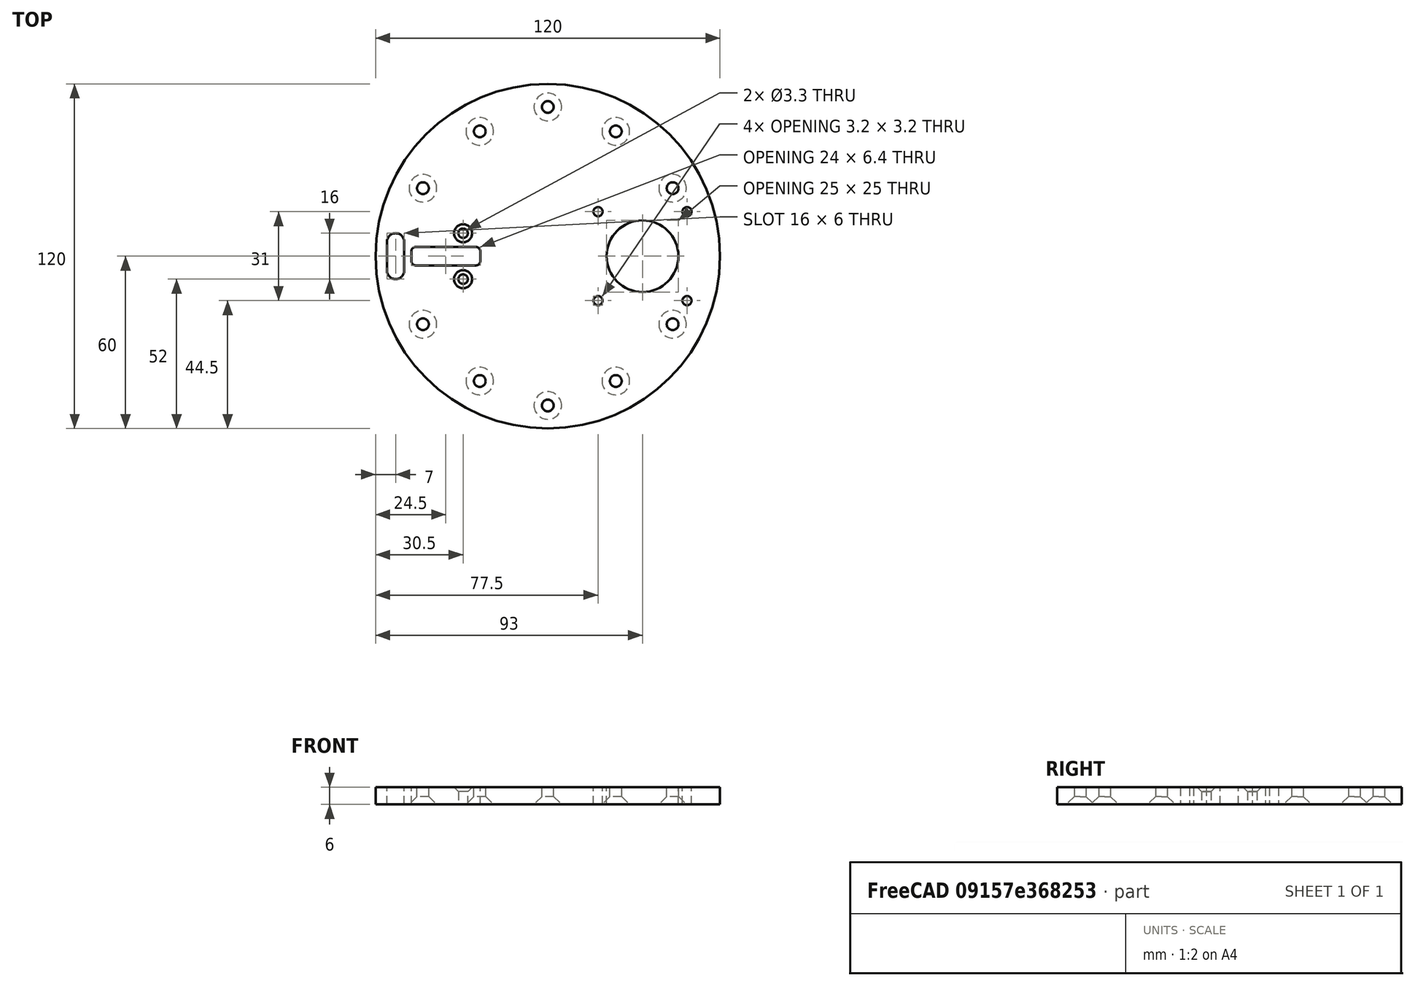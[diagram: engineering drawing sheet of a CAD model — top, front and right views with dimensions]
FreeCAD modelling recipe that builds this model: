
FCSTD DOCUMENT  (FreeCAD 0.19R24276 (Git))
Label: Z-axis_top_plate
License: All rights reserved
LicenseURL: http://en.wikipedia.org/wiki/All_rights_reserved
objects: Part::Part2DObjectPython×2, PartDesign::Chamfer×2, Sketcher::SketchObject×1, PartDesign::Pad×1, PartDesign::Fillet×1, PartDesign::Body×1
note: 12 computed .brp shape members not serialized (recipe doc carries the construction recipe); baked Part::Feature solids carry a one-line shape summary decoded from their .brp

FEATURE [Part::Part2DObjectPython] Shape2DView  # Draft 2D object (typed FeaturePython)
  FaceNumbers = [32]
  FuseArch = false
  HiddenLines = false
  InPlace = true
  Projection = (0,1,0)
  ProjectionMode = 0
  SegmentLength = 0.05
  Tessellation = false
  VisibleOnly = false
FEATURE [Sketcher::SketchObject] Sketch
  FullyConstrained = false
  MapMode = 5
  Support = -> [XY_Plane]
  sketch-geometry (42):
    g0: ArcOfCircle CenterX=0 CenterY=-52 CenterZ=0 NormalX=0 NormalY=0 NormalZ=1 AngleXU=0 Radius=2.05 StartAngle=3.14159 EndAngle=6.28319
    g1: ArcOfCircle CenterX=23.6881 CenterY=-43.4871 CenterZ=0 NormalX=0 NormalY=0 NormalZ=1 AngleXU=0 Radius=2.05 StartAngle=3.14159 EndAngle=6.28319
    g2: ArcOfCircle CenterX=43.4871 CenterY=-23.6881 CenterZ=0 NormalX=0 NormalY=0 NormalZ=1 AngleXU=0 Radius=2.05 StartAngle=3.14159 EndAngle=6.28319
    g3: ArcOfCircle CenterX=43.4871 CenterY=23.6881 CenterZ=0 NormalX=0 NormalY=0 NormalZ=1 AngleXU=0 Radius=2.05 StartAngle=3.14159 EndAngle=6.28319
    g4: ArcOfCircle CenterX=23.6881 CenterY=43.4871 CenterZ=0 NormalX=0 NormalY=0 NormalZ=1 AngleXU=0 Radius=2.05 StartAngle=3.14159 EndAngle=6.28319
    g5: ArcOfCircle CenterX=0 CenterY=52 CenterZ=0 NormalX=0 NormalY=0 NormalZ=1 AngleXU=0 Radius=2.05 StartAngle=3.14159 EndAngle=6.28319
    g6: ArcOfCircle CenterX=-23.6881 CenterY=43.4871 CenterZ=0 NormalX=0 NormalY=0 NormalZ=1 AngleXU=0 Radius=2.05 StartAngle=3.14159 EndAngle=6.28319
    g7: ArcOfCircle CenterX=-43.4871 CenterY=23.6881 CenterZ=0 NormalX=0 NormalY=0 NormalZ=1 AngleXU=0 Radius=2.05 StartAngle=3.14159 EndAngle=6.28319
    g8: ArcOfCircle CenterX=-43.4871 CenterY=-23.6881 CenterZ=0 NormalX=0 NormalY=0 NormalZ=1 AngleXU=0 Radius=2.05 StartAngle=3.14159 EndAngle=6.28319
    g9: ArcOfCircle CenterX=-23.6881 CenterY=-43.4871 CenterZ=0 NormalX=0 NormalY=0 NormalZ=1 AngleXU=0 Radius=2.05 StartAngle=3.14159 EndAngle=6.28319
    g10: ArcOfCircle CenterX=17.5 CenterY=-15.5 CenterZ=0 NormalX=0 NormalY=0 NormalZ=1 AngleXU=0 Radius=1.6 StartAngle=3.14159 EndAngle=6.28319
    g11: ArcOfCircle CenterX=17.5 CenterY=15.5 CenterZ=0 NormalX=0 NormalY=0 NormalZ=1 AngleXU=0 Radius=1.6 StartAngle=3.14159 EndAngle=6.28319
    g12: ArcOfCircle CenterX=48.5 CenterY=15.5 CenterZ=0 NormalX=0 NormalY=0 NormalZ=1 AngleXU=0 Radius=1.6 StartAngle=3.14159 EndAngle=6.28319
    g13: ArcOfCircle CenterX=48.5 CenterY=-15.5 CenterZ=0 NormalX=0 NormalY=0 NormalZ=1 AngleXU=0 Radius=1.6 StartAngle=3.14159 EndAngle=6.28319
    g14: ArcOfCircle CenterX=33 CenterY=0 CenterZ=0 NormalX=0 NormalY=0 NormalZ=1 AngleXU=0 Radius=12.5 StartAngle=3.14159 EndAngle=6.28319
    g15: ArcOfCircle CenterX=0 CenterY=0 CenterZ=0 NormalX=0 NormalY=0 NormalZ=1 AngleXU=0 Radius=60 StartAngle=0 EndAngle=3.14159
    g16: ArcOfCircle CenterX=0 CenterY=0 CenterZ=0 NormalX=0 NormalY=0 NormalZ=1 AngleXU=0 Radius=60 StartAngle=3.14159 EndAngle=6.28319
    g17: ArcOfCircle CenterX=17.5 CenterY=-15.5 CenterZ=0 NormalX=0 NormalY=0 NormalZ=1 AngleXU=0 Radius=1.6 StartAngle=0 EndAngle=3.14159
    g18: ArcOfCircle CenterX=17.5 CenterY=15.5 CenterZ=0 NormalX=0 NormalY=0 NormalZ=1 AngleXU=0 Radius=1.6 StartAngle=0 EndAngle=3.14159
    g19: ArcOfCircle CenterX=48.5 CenterY=15.5 CenterZ=0 NormalX=0 NormalY=0 NormalZ=1 AngleXU=0 Radius=1.6 StartAngle=0 EndAngle=3.14159
    g20: ArcOfCircle CenterX=48.5 CenterY=-15.5 CenterZ=0 NormalX=0 NormalY=0 NormalZ=1 AngleXU=0 Radius=1.6 StartAngle=0 EndAngle=3.14159
    g21: ArcOfCircle CenterX=33 CenterY=0 CenterZ=0 NormalX=0 NormalY=0 NormalZ=1 AngleXU=0 Radius=12.5 StartAngle=0 EndAngle=3.14159
    g22: ArcOfCircle CenterX=43.4871 CenterY=-23.6881 CenterZ=0 NormalX=0 NormalY=0 NormalZ=1 AngleXU=0 Radius=2.05 StartAngle=0 EndAngle=3.14159
    g23: ArcOfCircle CenterX=23.6881 CenterY=-43.4871 CenterZ=0 NormalX=0 NormalY=0 NormalZ=1 AngleXU=0 Radius=2.05 StartAngle=0 EndAngle=3.14159
    g24: ArcOfCircle CenterX=-43.4871 CenterY=-23.6881 CenterZ=0 NormalX=0 NormalY=0 NormalZ=1 AngleXU=0 Radius=2.05 StartAngle=0 EndAngle=3.14159
    g25: ArcOfCircle CenterX=23.6881 CenterY=43.4871 CenterZ=0 NormalX=0 NormalY=0 NormalZ=1 AngleXU=0 Radius=2.05 StartAngle=0 EndAngle=3.14159
    g26: ArcOfCircle CenterX=-23.6881 CenterY=-43.4871 CenterZ=0 NormalX=0 NormalY=0 NormalZ=1 AngleXU=0 Radius=2.05 StartAngle=0 EndAngle=3.14159
    g27: ArcOfCircle CenterX=-23.6881 CenterY=43.4871 CenterZ=0 NormalX=0 NormalY=0 NormalZ=1 AngleXU=0 Radius=2.05 StartAngle=0 EndAngle=3.14159
    g28: ArcOfCircle CenterX=-43.4871 CenterY=23.6881 CenterZ=0 NormalX=0 NormalY=0 NormalZ=1 AngleXU=0 Radius=2.05 StartAngle=0 EndAngle=3.14159
    g29: ArcOfCircle CenterX=43.4871 CenterY=23.6881 CenterZ=0 NormalX=0 NormalY=0 NormalZ=1 AngleXU=0 Radius=2.05 StartAngle=0 EndAngle=3.14159
    g30: ArcOfCircle CenterX=0 CenterY=52 CenterZ=0 NormalX=0 NormalY=0 NormalZ=1 AngleXU=0 Radius=2.05 StartAngle=0 EndAngle=3.14159
    g31: ArcOfCircle CenterX=0 CenterY=-52 CenterZ=0 NormalX=0 NormalY=0 NormalZ=1 AngleXU=0 Radius=2.05 StartAngle=0 EndAngle=3.14159
    g32: LineSegment StartX=-47.5 StartY=3.2 StartZ=0 EndX=-23.5 EndY=3.2 EndZ=0
    g33: LineSegment StartX=-23.5 StartY=3.2 StartZ=0 EndX=-23.5 EndY=-3.2 EndZ=0
    g34: LineSegment StartX=-23.5 StartY=-3.2 StartZ=0 EndX=-47.5 EndY=-3.2 EndZ=0
    g35: LineSegment StartX=-47.5 StartY=-3.2 StartZ=0 EndX=-47.5 EndY=3.2 EndZ=0
    g36: Circle CenterX=-29.5 CenterY=8 CenterZ=0 NormalX=0 NormalY=0 NormalZ=1 AngleXU=0 Radius=1.65
    g37: Circle CenterX=-29.5 CenterY=-8 CenterZ=0 NormalX=0 NormalY=0 NormalZ=1 AngleXU=0 Radius=1.65
    g38: ArcOfCircle CenterX=-53 CenterY=5 CenterZ=0 NormalX=0 NormalY=0 NormalZ=1 AngleXU=0 Radius=3 StartAngle=2e-16 EndAngle=3.14159
    g39: ArcOfCircle CenterX=-53 CenterY=-5 CenterZ=0 NormalX=0 NormalY=0 NormalZ=1 AngleXU=0 Radius=3 StartAngle=3.14159 EndAngle=6.28319
    g40: LineSegment StartX=-56 StartY=5 StartZ=0 EndX=-56 EndY=-5 EndZ=0
    g41: LineSegment StartX=-50 StartY=5 StartZ=0 EndX=-50 EndY=-5 EndZ=0
  constraints (26):
    c: Coincident(g32,g33)
    c: Coincident(g33,g34)
    c: Coincident(g34,g35)
    c: Coincident(g35,g32)
    c: Horizontal(g32)
    c: Horizontal(g34)
    c: Vertical(g35)
    c: Symmetric(g32,g33,g-1)
    c: DistanceX(g32,g32) = 24
    c: DistanceY(g35,g35) = 6.4
    c: Radius(g15) = 60
    c: Equal(g36,g37)
    c: Symmetric(g37,g36,g-1)
    c: Radius(g36) = 1.65
    c: DistanceX(g36,g32) = 6
    c: Tangent(g38,g41) = 1.5708
    c: Tangent(g38,g40) = -1.5708
    c: Tangent(g40,g39) = -1.5708
    c: Tangent(g41,g39) = 1.5708
    c: Vertical(g40)
    c: Radius(g38) = 3
    c: DistanceY(g41,g41) = 10
    c: Symmetric(g38,g39,g-1)
    c: DistanceX(g38) = -50
    c: DistanceX(g33) = -23.5
    c: DistanceY(g36) = 8
FEATURE [PartDesign::Pad] Pad
  Direction = (1,1,1)
  Length = 6
  Length2 = 100
  Profile = -> Sketch
  Type = 0
FEATURE [PartDesign::Chamfer] Chamfer
  Angle = 45
  Base = -> Pad [Edge41,Edge65,Edge47,Edge89,Edge95,Edge53,Edge71,Edge59,Edge77,Edge83]
  BaseFeature = -> Pad
  ChamferType = 0
  FlipDirection = false
  Size = 2.75
  Size2 = 1
  SupportTransform = false
FEATURE [PartDesign::Chamfer] Chamfer001
  Angle = 45
  Base = -> Chamfer [Edge41,Edge40]
  BaseFeature = -> Chamfer
  ChamferType = 0
  FlipDirection = false
  Size = 1.5
  Size2 = 1
  SupportTransform = false
FEATURE [PartDesign::Fillet] Fillet
  Base = -> Chamfer001 [Edge54,Edge56,Edge53,Edge58]
  BaseFeature = -> Chamfer001
  Radius = 1.5
  SupportTransform = false
FEATURE [PartDesign::Body] Body
  Group = -> [Sketch,Pad,Chamfer,Chamfer001,Fillet]
  Origin = -> Origin
  Tip = -> Fillet
FEATURE [Part::Part2DObjectPython] Shape2DView001  # Draft 2D object (typed FeaturePython)
  Base = -> Fillet
  FaceNumbers = [47]
  FuseArch = false
  HiddenLines = false
  InPlace = true
  Projection = (0,0,-1)
  ProjectionMode = 0
  SegmentLength = 0.05
  Tessellation = false
  VisibleOnly = false
